# Revit family: 2_Way_Diverter_Trim-Grohe-Eurocube-29218001
name_source: partatom
category: Plumbing Fixtures
revit_build: Autodesk Revit 2018 (Build: 20170223_1515(x64)
units: mm (PartAtom-declared; Revit-internal decimal feet)

## family parameters
Cut with Voids When Loaded = No
Host = Face
OmniClass Number = 23.45.05.14.17
OmniClass Title = Showers
Part Type = Normal
Room Calculation Point = No
Round Connector Dimension = Use Diameter
Shared = Yes

## types (1)
- 29218001
    ADA Compliant = Yes
    Assembly Code = D2020300
    CW Connection = Yes
    CWFU = 3
    Default Elevation = 0"
    Description = EUROCUBE 2-Way Shower Diverter
    Finish = Metal-Grohe-001-Starlight Chrome
    HW Connection = Yes
    HWFU = 3
    Height = 4 1/2"
    Installation Type = Wall Mounted
    Length = 2 3/16"
    Manufacturer = Grohe
    Material = Metal-Grohe-001-Chrome
    Model = 29218001
    Price = Prices may vary. Please consult Manufacturer Representative for most up-to-date price list.
    Product Documentation Link = https://americanstandard.box.com
    Product Page URL = https://www.grohe.us
    URL = https://www.grohe.us
    Vent Connection = No
    WFU = 4
    Warranty Information = Limited Lifetime Warranty
    Waste Connection = No
    Width = 3 15/16"

## geometry (parser evidence)
native form markers: Sweep x3
no freeform markers — native parametric forms only
